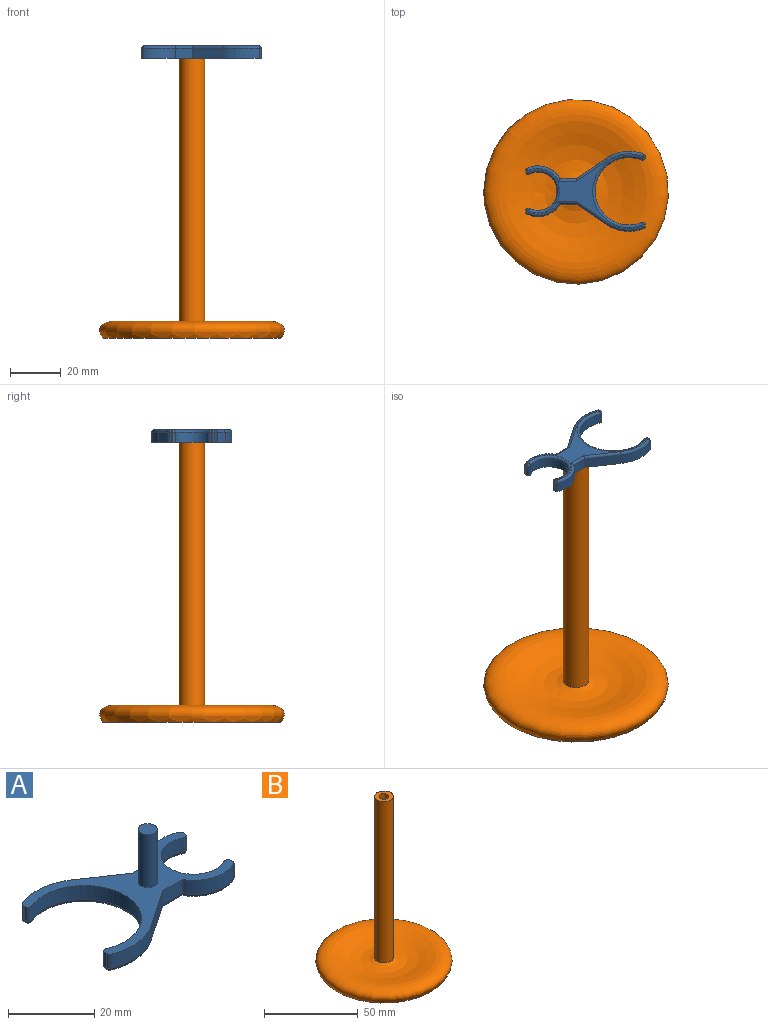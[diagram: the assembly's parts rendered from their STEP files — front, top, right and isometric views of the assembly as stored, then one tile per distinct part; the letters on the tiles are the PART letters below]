
ASSEMBLY  parts=2 mates=1
PART A: 48 faces, bbox 47x34.1x20 mm
  f0: cylinder r=10mm len=12.89mm, axis (0,0,-1), area 59.4mm2, adj f4,f12,f19,f35
  f1: torus R=9mm, axis (0,0,1), area 22.8mm2, adj f3,f10,f21,f33
  f2: cylinder r=15.75mm len=14.63mm, axis (0,0,-1), area 61.2mm2, adj f7,f12,f25,f44
  f3: plane 45.01x29.5mm, normal (0,0,-1), area 185.1mm2, adj f1,f17,f18,f19,f20,f21,f22,f23
  f4: plane 6.34x4mm, normal (0,1,0), area 25.4mm2, adj f0,f5,f12,f17
  f5: plane 11.94x8.06mm, normal (0.56,0.83,0), area 57.6mm2, adj f4,f6,f12,f18
  f6: cylinder r=15.75mm len=14.63mm, axis (0,0,-1), area 61.2mm2, adj f5,f12,f20,f40
  f7: plane 11.94x8.06mm, normal (0.56,-0.83,0), area 57.6mm2, adj f2,f8,f12,f23
  f8: plane 6.34x4mm, normal (0,-1,0), area 25.4mm2, adj f7,f10,f12,f21
  f9: cylinder r=7.5mm len=15mm, axis (0,0,-1), area 122.1mm2, adj f12,f27,f30,f36
  f10: cylinder r=10mm len=12.89mm, axis (0,0,-1), area 59.4mm2, adj f1,f8,f12,f34
  f11: cylinder r=13.25mm len=26.5mm, axis (0,0,-1), area 208.1mm2, adj f12,f24,f42,f46
  f12: plane 47.01x31.5mm, normal (0,0,1), area 365.3mm2, adj f0,f2,f4,f5,f6,f7,f8,f9
  f13: cylinder r=2.25mm len=15mm, axis (0,0,-1), area 212.1mm2, adj f12,f14
  f14: plane 4.5x4.5mm, normal (0,0,1), area 15.9mm2, adj f13
  f15: plane 4x0.54mm, normal (-1,0,0), area 2.2mm2, adj f12,f22,f40,f42
  f16: plane 4x0.54mm, normal (-1,0,0), area 2.2mm2, adj f12,f26,f44,f46
  f17: cylinder r=1mm len=7.24mm, axis (-1,0,0), area 10.5mm2, adj f3,f4,f18,f19
  f18: cylinder r=1mm len=12.75mm, axis (-0.83,0.56,0), area 22.8mm2, adj f3,f5,f17,f20
  f19: torus R=9mm, axis (0,0,1), area 22.8mm2, adj f0,f3,f17,f37
  f20: torus R=14.75mm, axis (0,0,1), area 23.5mm2, adj f3,f6,f18,f41
  f21: cylinder r=1mm len=7.24mm, axis (1,0,0), area 10.5mm2, adj f1,f3,f8,f23
  f22: cylinder r=1mm len=1mm, axis (0,-1,0), area 0.8mm2, adj f3,f15,f41,f43
  f23: cylinder r=1mm len=12.75mm, axis (0.83,0.56,0), area 22.8mm2, adj f3,f7,f21,f25
  f24: torus R=14.25mm, axis (0,0,1), area 84mm2, adj f3,f11,f43,f47
  f25: torus R=14.75mm, axis (0,0,1), area 23.5mm2, adj f2,f3,f23,f45
  f26: cylinder r=1mm len=1mm, axis (0,-1,0), area 0.8mm2, adj f3,f16,f45,f47
  f27: torus R=8.5mm, axis (0,0,1), area 50.3mm2, adj f3,f9,f31,f38
  f28: plane 4x0.56mm, normal (1,0,0), area 2.2mm2, adj f12,f35,f36,f39
  f29: plane 4x0.56mm, normal (1,0,0), area 2.2mm2, adj f12,f30,f32,f34
  f30: cylinder r=1mm len=4mm, axis (0,0,-1), area 8.1mm2, adj f9,f12,f29,f31
  f31: sphere r=1mm, area 2mm2, adj f27,f30,f32
  f32: cylinder r=1mm len=1mm, axis (0,-1,0), area 0.9mm2, adj f3,f29,f31,f33
  f33: sphere r=1mm, area 1.1mm2, adj f1,f32,f34
  f34: cylinder r=1mm len=4mm, axis (0,0,-1), area 4.5mm2, adj f10,f12,f29,f33
  f35: cylinder r=1mm len=4mm, axis (0,0,-1), area 4.5mm2, adj f0,f12,f28,f37
  f36: cylinder r=1mm len=4mm, axis (0,0,-1), area 8.1mm2, adj f9,f12,f28,f38
  f37: sphere r=1mm, area 1.1mm2, adj f19,f35,f39
  f38: sphere r=1mm, area 2mm2, adj f27,f36,f39
  f39: cylinder r=1mm len=1mm, axis (0,-1,0), area 0.9mm2, adj f3,f28,f37,f38
  f40: cylinder r=1mm len=4mm, axis (0,0,-1), area 4.8mm2, adj f6,f12,f15,f41
  f41: sphere r=1mm, area 1.2mm2, adj f20,f22,f40
  f42: cylinder r=1mm len=4mm, axis (0,0,-1), area 7.9mm2, adj f11,f12,f15,f43
  f43: sphere r=1mm, area 2mm2, adj f22,f24,f42
  f44: cylinder r=1mm len=4mm, axis (0,0,-1), area 4.8mm2, adj f2,f12,f16,f45
  f45: sphere r=1mm, area 1.2mm2, adj f25,f26,f44
  f46: cylinder r=1mm len=4mm, axis (0,0,-1), area 7.9mm2, adj f11,f12,f16,f47
  f47: sphere r=1mm, area 2mm2, adj f24,f26,f46
PART B: 6 faces, bbox 72.7x72.7x110 mm
  f0: revolved ~72.66x72.66mm, area 5289.3mm2, adj f1,f3
  f1: plane 70x70mm, normal (0,0,-1), area 3848.5mm2, adj f0
  f2: plane 10x10mm, normal (0,0,1), area 58.9mm2, adj f3,f4
  f3: cylinder r=5mm len=105mm, axis (0,0,-1), area 3298.7mm2, adj f0,f2
  f4: cylinder r=2.5mm len=15mm, axis (0,0,1), area 235.6mm2, adj f2,f5
  f5: plane 5x5mm, normal (0,0,1), area 19.6mm2, adj f4
PLACE A rot(axis=(0,1,0),180deg) t=(0,0,113)mm
PLACE B t=(0,0,-2)mm
MATE fastened A.f13 <-> B.f3  axis (0,0,-1) through (0,0,93)mm
